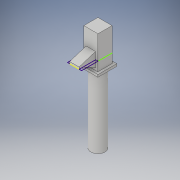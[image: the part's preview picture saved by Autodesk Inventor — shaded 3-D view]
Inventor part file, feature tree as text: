
AUTODESK INVENTOR PART (.ipt)
format: ipt  version: 2019 (Build 230136000, 136)  size: 228,352 bytes
history: native  units: in
note: dims shown in document units (in); Inventor stores cm internally (conversion verified against a paired STEP export)
features: extrude x12, sketch x10, fillet x3
ambient origin geometry x8: Origin, YZ Plane, XZ Plane, XY Plane, X Axis, Y Axis, Z Axis, Center Point
bodies: Solid1 (feature_tree)
feature tree (25):
  sketch  "Sketch1"  dims[d0=0.2362in d1=0.3937in d2=0.0in]
  extrude  "Extrusion1"  Depth=0.3937in TaperAngle=0.0deg
  extrude  "Extrusion2"  Depth=0.1181in
  extrude  "Extrusion3"  Depth=1.1811in
  extrude  "Extrusion4"  Depth=0.1575in
  fillet  "Fillet1"  Radius=0.3937in
  fillet  "Fillet2"  [1 undecoded]
  fillet  "Fillet3"  Radius=0.0197in
  extrude  "Extrusion5"  Depth=0.0394in
  sketch  "Sketch5"  dims[d15=0.0394in d16=0.0394in]
  extrude  "Extrusion6"  Depth=0.2362in
  extrude  "Extrusion7"  Depth=0.0394in
  extrude  "Extrusion8"  Depth=0.3937in TaperAngle=0.0deg
  sketch  "Sketch6"  dims[d17=0.3937in d18=0.0in d19=0.2362in]
  sketch  "Sketch7"  dims[d20=0.0394in d21=0.0394in]
  extrude  "Extrusion9"  Depth=0.1969in
  extrude  "Extrusion10"  Depth=0.1969in TaperAngle=0.0deg
  extrude  "Extrusion11"  Depth=0.0394in
  extrude  "Extrusion12"  Depth=0.0394in
  sketch  "Sketch2"  dims[d3=0.7874in d4=0.0in d5=0.1181in]
  sketch  "Sketch3"  dims[d6=0.2362in d7=1.1811in]
  sketch  "Sketch4"  dims[d8=0.2756in d9=0.0in d10=0.1575in d11=0.3937in d12=0.0in d13=0.0in d14=0.0197in]
  sketch  "Sketch9"  dims[d22=0.3937in d23=0.0in d24=0.3937in d25=0.0in]
  sketch  "Sketch10"  dims[d26=0.1969in d27=0.0in d28=0.0591in]
  sketch  "Sketch11"  dims[d29=0.1181in d30=0.0in d31=0.1969in d32=0.0in d33=0.0394in d34=0.0394in d35=0.0394in d36=0.0394in d37=0.0394in d38=0.0in d39=0.2362in d40=0.5906in d41=0.0in]
note: 1 required parameter value undecoded (feature->parameter linkage not recoverable at this tier; creation-order binding heuristic only, values carry confidence <= 0.55)
